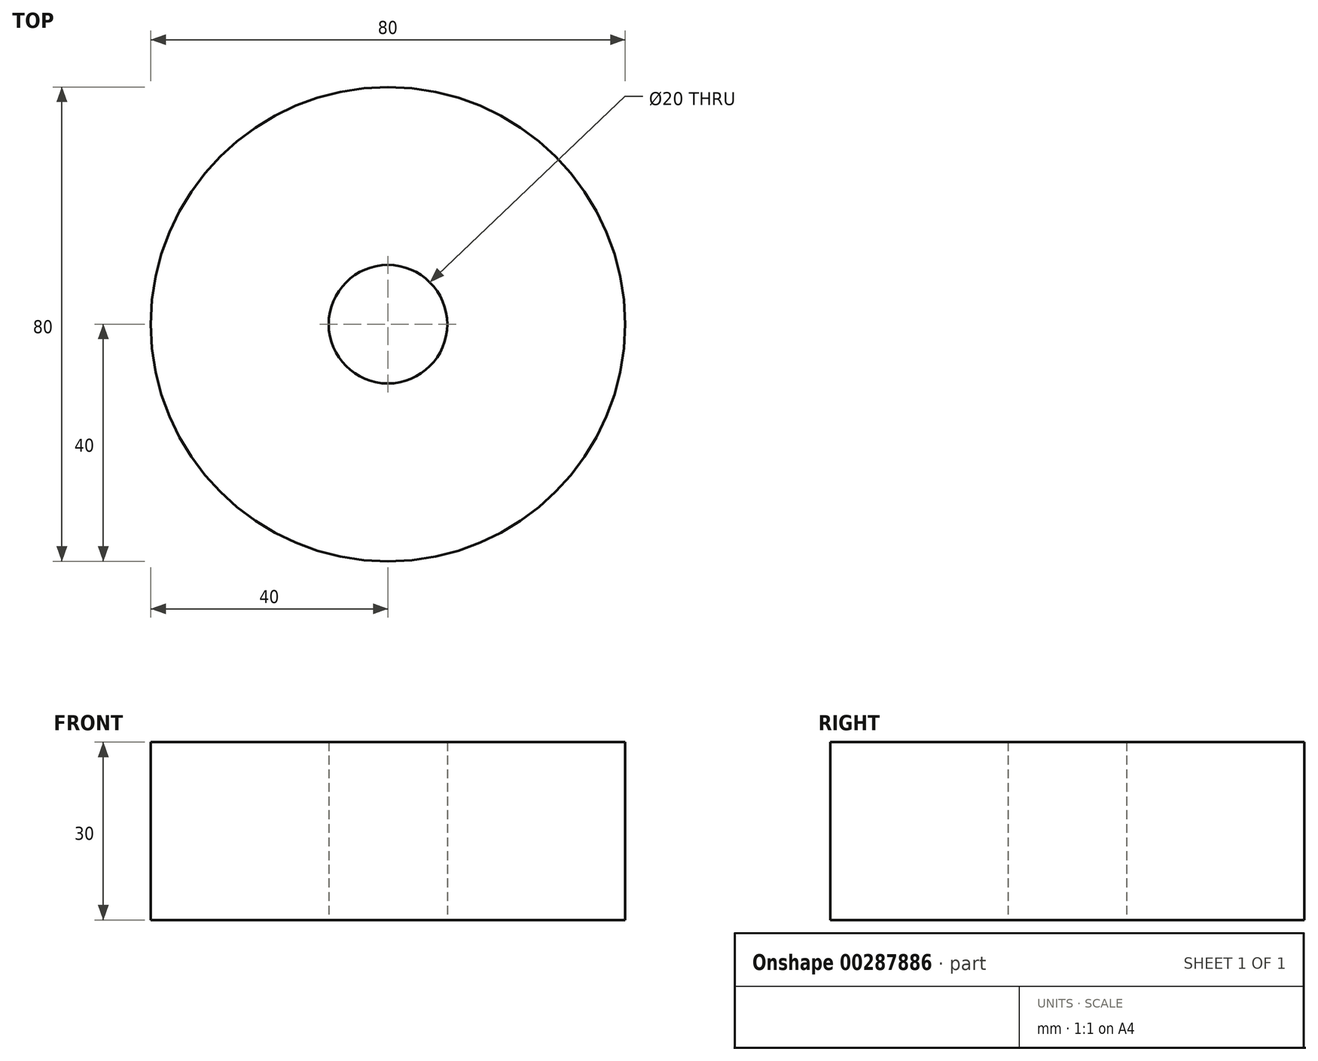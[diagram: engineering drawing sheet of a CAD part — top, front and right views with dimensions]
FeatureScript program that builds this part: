
annotation { "Feature Type Name" : "Feature", "Feature Type Description" : "" }
export const myFeature = defineFeature(function(context is Context, id is Id, definition is map)
    precondition{}
    {
        {
            var Q0;
            Q0=qCreatedBy(makeId("Top.planeOp"),FACE);
            var sketch = newSketch(context, id + "F0", { "sketchPlane" : qUnion([Q0])});
            skCircle(sketch, "E0", {"center": v(0, 0) * mm, "radius": 40 * mm});
            skCircle(sketch, "E1", {"center": v(0, 0) * mm, "radius": 10 * mm});
            skSolve(sketch);
        }
        {
            var Q0;
            Q0 = qSketchRegion(id + "F0", true);
            extrude(context, id + "F1", {"entities" : qUnion([Q0]), "depth" : 30 * mm});
        }
    });
